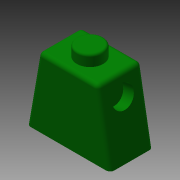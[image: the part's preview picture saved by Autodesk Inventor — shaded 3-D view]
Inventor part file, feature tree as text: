
AUTODESK INVENTOR PART (.ipt)
format: ipt  version: 2015 (Build 190159000, 159)  size: 161,792 bytes
history: native  units: mm
features: extrude x4, sketch x4, fillet x3, mirror x1
ambient origin geometry x8: Origin, YZ Plane, XZ Plane, XY Plane, X Axis, Y Axis, Z Axis, Center Point
bodies: Solid1 (feature_tree)
feature tree (12):
  extrude  "Extrusion1"  Depth=13.962634mm
  extrude  "Extrusion2"  Depth=8.0mm TaperAngle=0.0deg
  extrude  "Extrusion3"  Depth=8.0mm
  fillet  "Fillet1"  Radius=6.0mm
  fillet  "Fillet2"  Radius=4.88mm
  fillet  "Fillet3"  Radius=2.0mm
  extrude  "Extrusion4"  Depth=0.75mm
  mirror  "Mirror1"
  sketch  "Sketch1"  dims[d0=15.44mm d1=13.962634mm]
  sketch  "Sketch2"  dims[d2=12.77mm d3=8.0mm d4=0.0mm]
  sketch  "Sketch3"  dims[d5=5.0mm d6=8.0mm d7=6.0mm d8=0.0mm d9=4.88mm d10=2.0mm d11=0.0mm]
  sketch  "Sketch4"  dims[d12=0.4mm d13=0.75mm d14=0.75mm d15=4.0mm d16=9.5mm d17=2.0mm d18=0.0mm]
